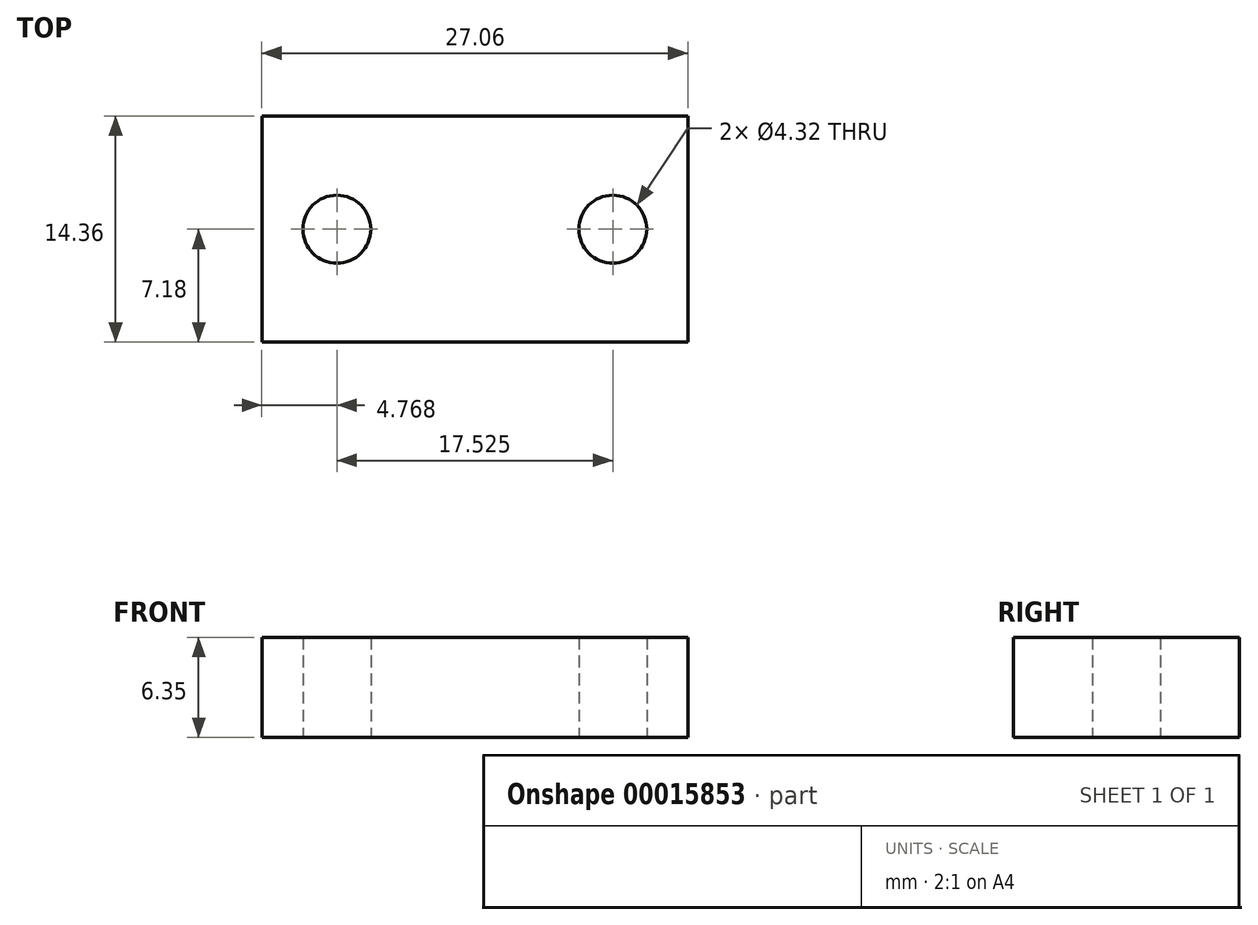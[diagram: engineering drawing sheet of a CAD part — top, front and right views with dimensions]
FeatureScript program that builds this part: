
annotation { "Feature Type Name" : "Feature", "Feature Type Description" : "" }
export const myFeature = defineFeature(function(context is Context, id is Id, definition is map)
    precondition{}
    {
        {
            var Q0;
            Q0=qCreatedBy(makeId("Top.planeOp"),FACE);
            var sketch = newSketch(context, id + "F0", { "sketchPlane" : qUnion([Q0])});
            skLineSegment(sketch, "E0.rect.bottom", {"start": v(13.53, -7.18) * mm, "end": v(-13.53, -7.18) * mm});
            skLineSegment(sketch, "E0.rect.top", {"start": v(13.53, 7.18) * mm, "end": v(-13.53, 7.18) * mm});
            skLineSegment(sketch, "E0.rect.left", {"start": v(13.53, -7.18) * mm, "end": v(13.53, 7.18) * mm});
            skLineSegment(sketch, "E0.rect.right", {"start": v(-13.53, -7.18) * mm, "end": v(-13.53, 7.18) * mm});
            skPoint(sketch, "E0.rect.middle", {"position": v(0, 0) * mm});
            skLineSegment(sketch, "E1", {"start": v(-13.53, 0) * mm, "end": v(-8.76, 0) * mm});
            skLineSegment(sketch, "E2", {"start": v(13.53, 0) * mm, "end": v(8.76, 0) * mm});
            skCircle(sketch, "E3", {"center": v(-8.76, 0) * mm, "radius": 2.16 * mm});
            skCircle(sketch, "E4", {"center": v(8.76, 0) * mm, "radius": 2.16 * mm});
            skSolve(sketch);
        }
        {
            var Q0;
            Q0=qSketchRegion(id+"F0",true);
            extrude(context, id + "F1", {"entities" : qUnion([Q0]), "depth" : 6.35 * mm});
        }
    });
